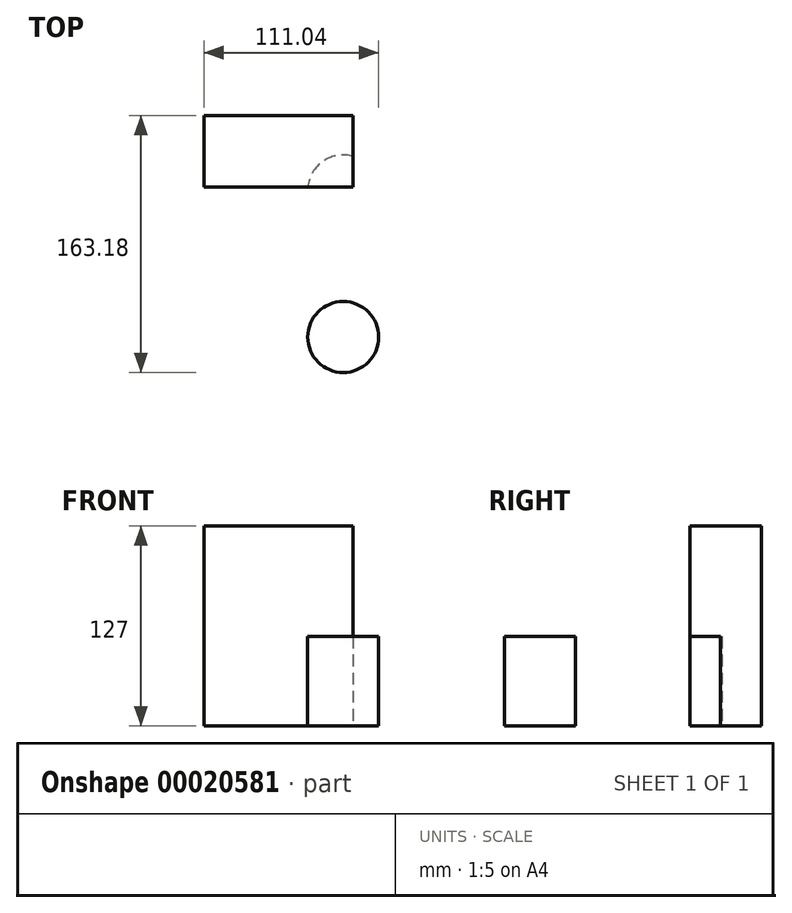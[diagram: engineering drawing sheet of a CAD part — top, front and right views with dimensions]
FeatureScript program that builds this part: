
annotation { "Feature Type Name" : "Feature", "Feature Type Description" : "" }
export const myFeature = defineFeature(function(context is Context, id is Id, definition is map)
    precondition{}
    {
        {
            var Q0;
            Q0=qCreatedBy(makeId("Top.planeOp"),FACE);
            var sketch = newSketch(context, id + "F0", { "sketchPlane" : qUnion([Q0])});
            skLineSegment(sketch, "E0.rect.bottom", {"start": v(47.44, -22.7) * mm, "end": v(-47.44, -22.7) * mm});
            skLineSegment(sketch, "E0.rect.top", {"start": v(47.44, 22.7) * mm, "end": v(-47.44, 22.7) * mm});
            skLineSegment(sketch, "E0.rect.left", {"start": v(47.44, -22.7) * mm, "end": v(47.44, 22.7) * mm});
            skLineSegment(sketch, "E0.rect.right", {"start": v(-47.44, -22.7) * mm, "end": v(-47.44, 22.7) * mm});
            skPoint(sketch, "E0.rect.middle", {"position": v(0, 0) * mm});
            skSolve(sketch);
        }
        {
            var Q0;
            Q0 = qSketchRegion(id + "F0", true);
            extrude(context, id + "F1", {"entities" : qUnion([Q0]), "depth" : 127 * mm});
        }
        {
            var Q0;
            Q0=qCreatedBy(makeId("Top.planeOp"),FACE);
            var sketch = newSketch(context, id + "F2", { "sketchPlane" : qUnion([Q0])});
            skCircle(sketch, "E1", {"center": v(-13.11, -49.39) * mm, "radius": 22.54 * mm});
            skSolve(sketch);
        }
        {
            var Q0;
            Q0 = qSketchRegion(id + "F2", true);
            extrude(context, id + "F3", {"entities" : qUnion([Q0]), "depth" : 56.8 * mm});
        }
        {
            var Q0;
            Q0=makeQuery(id+"F3.opExtrude","SWEPT_BODY",BODY,{"disambiguationData":[OSD([sQuery(id+"F2.wireOp",EDGE,"E1")])]});
            transform(context, id + "F4", {"entities" : qUnion([Q0]), "transformType" : TransformType.TRANSLATION_3D, "dx" : 54.17 * mm, "dy" : 24.5 * mm, "dz" : 0 * mm, "makeCopy" : false});
        }
        {
            var Q0;
            Q0=makeQuery(id+"F3.opExtrude","SWEPT_BODY",BODY,{"disambiguationData":[OSD([sQuery(id+"F2.wireOp",EDGE,"E1")])]});
            var Q1;
            Q1=makeQuery(id+"F1.opExtrude","SWEPT_BODY",BODY,{"disambiguationData":[OSD([sQuery(id+"F0.wireOp",EDGE,"E0.rect.bottom"),sQuery(id+"F0.wireOp",EDGE,"E0.rect.top"),sQuery(id+"F0.wireOp",EDGE,"E0.rect.left"),sQuery(id+"F0.wireOp",EDGE,"E0.rect.right")])]});
            booleanBodies(context, id + "F5", {"operationType" : BooleanOperationType.SUBTRACTION, "tools" : qUnion([Q0]), "targets" : qUnion([Q1]), "keepTools" : true});
        }
        {
            var Q0;
            Q0=makeQuery(id+"F3.opExtrude","SWEPT_BODY",BODY,{"disambiguationData":[OSD([sQuery(id+"F2.wireOp",EDGE,"E1")])]});
            transform(context, id + "F6", {"entities" : qUnion([Q0]), "transformType" : TransformType.TRANSLATION_3D, "dx" : 0 * mm, "dy" : -93.03 * mm, "dz" : 0 * mm, "makeCopy" : false});
        }
    });
